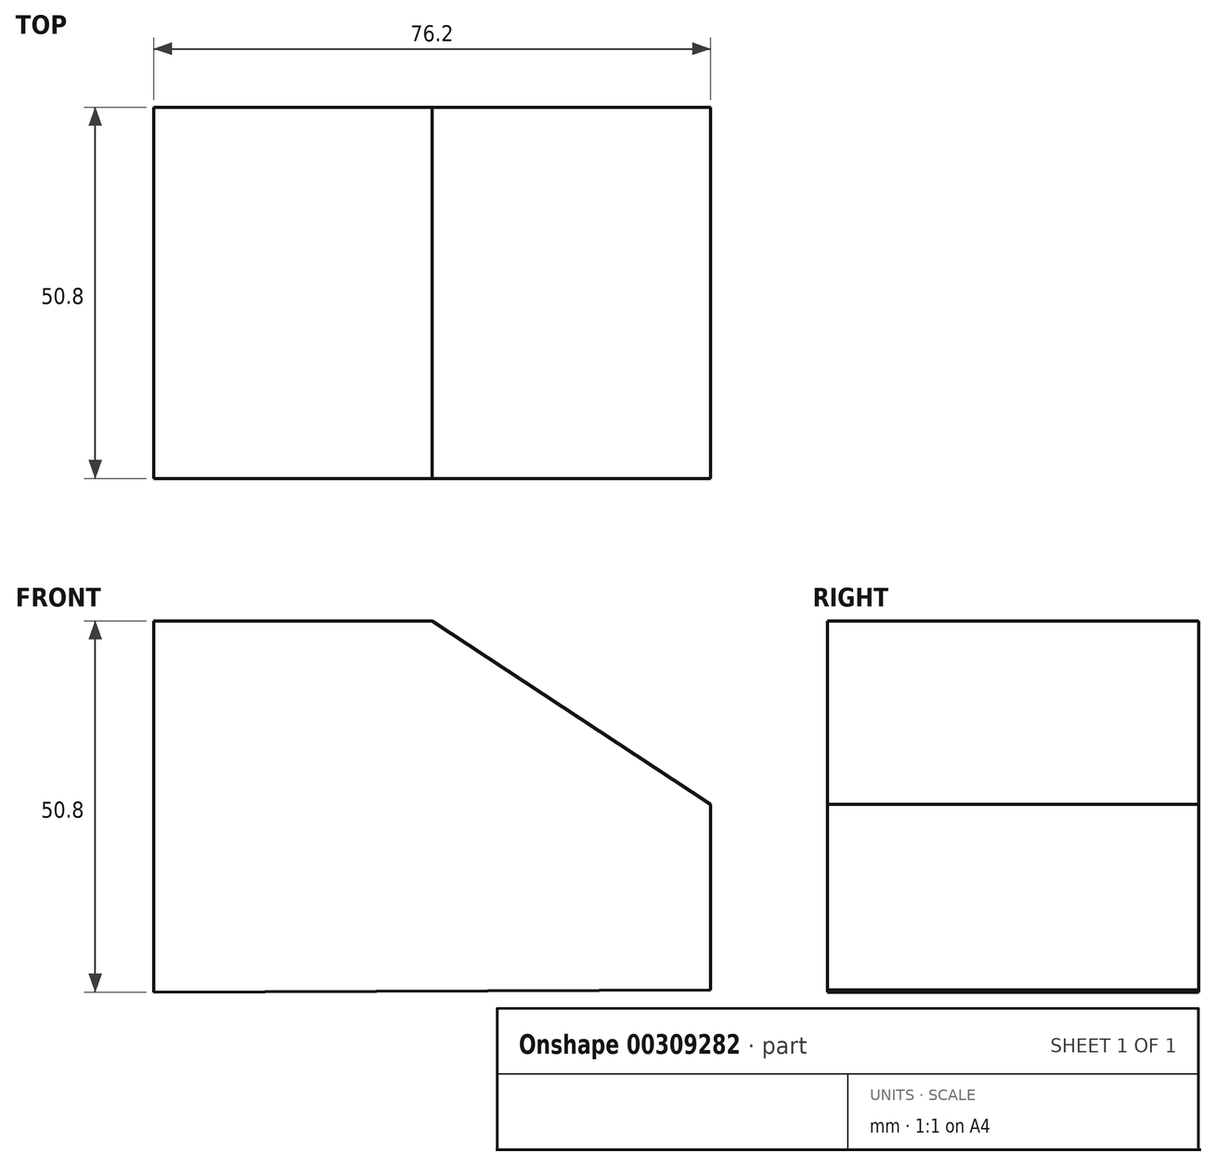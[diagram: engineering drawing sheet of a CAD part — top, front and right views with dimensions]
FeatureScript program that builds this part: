
annotation { "Feature Type Name" : "Feature", "Feature Type Description" : "" }
export const myFeature = defineFeature(function(context is Context, id is Id, definition is map)
    precondition{}
    {
        {
            var Q0;
            Q0=qCreatedBy(makeId("Front.planeOp"),FACE);
            var sketch = newSketch(context, id + "F0", { "sketchPlane" : qUnion([Q0])});
            skLineSegment(sketch, "E0", {"start": v(38.24, -44.94) * mm, "end": v(38.24, -19.54) * mm});
            skLineSegment(sketch, "E1", {"start": v(38.24, -19.54) * mm, "end": v(0.14, 5.58) * mm});
            skLineSegment(sketch, "E2", {"start": v(0.14, 5.58) * mm, "end": v(-37.96, 5.58) * mm});
            skLineSegment(sketch, "E3", {"start": v(-37.96, 5.58) * mm, "end": v(-37.96, -45.22) * mm});
            skLineSegment(sketch, "E4", {"start": v(-37.96, -45.22) * mm, "end": v(38.24, -44.94) * mm});
            skSolve(sketch);
        }
        {
            var Q0;
            Q0=makeQuery(id+"F0.imprint","IMPRINT",FACE,{"disambiguationData":[TD([[makeQuery(id+"F0.imprint","IMPRINT",EDGE,{"derivedFrom":sQuery(id+"F0.wireOp",EDGE,"E0")}),1.0]])]});
            extrude(context, id + "F1", {"entities" : qUnion([Q0]), "depth" : 50.8 * mm});
        }
    });
